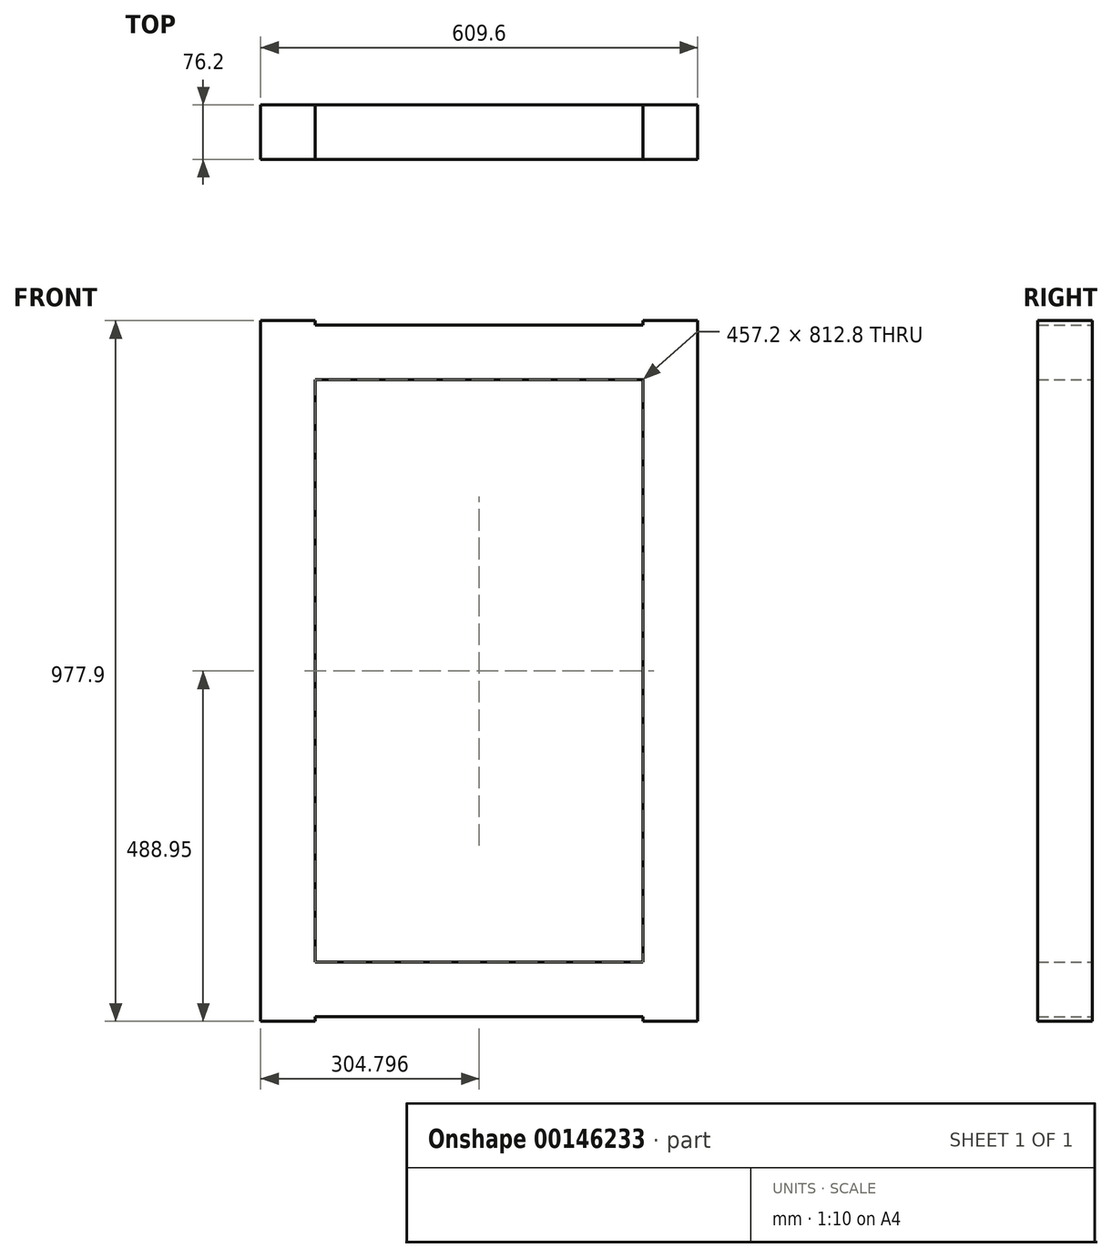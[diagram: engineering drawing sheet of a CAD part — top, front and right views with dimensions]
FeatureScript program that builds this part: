
annotation { "Feature Type Name" : "Feature", "Feature Type Description" : "" }
export const myFeature = defineFeature(function(context is Context, id is Id, definition is map)
    precondition{}
    {
        {
            var Q0;
            Q0=qCreatedBy(makeId("Top.planeOp"),FACE);
            var sketch = newSketch(context, id + "F0", { "sketchPlane" : qUnion([Q0])});
            skLineSegment(sketch, "E0.bottom", {"start": v(-224.13, 41.12) * mm, "end": v(233.07, 41.12) * mm});
            skLineSegment(sketch, "E0.top", {"start": v(-224.13, -35.08) * mm, "end": v(233.07, -35.08) * mm});
            skLineSegment(sketch, "E0.left", {"start": v(-224.13, 41.12) * mm, "end": v(-224.13, -35.08) * mm});
            skLineSegment(sketch, "E0.right", {"start": v(233.07, 41.12) * mm, "end": v(233.07, -35.08) * mm});
            skSolve(sketch);
        }
        {
            var Q0;
            Q0=makeQuery(id+"F0.imprint","IMPRINT",FACE,{"disambiguationData":[TD([[makeQuery(id+"F0.imprint","IMPRINT",EDGE,{"derivedFrom":sQuery(id+"F0.wireOp",EDGE,"E0.bottom")}),-1.0]])]});
            extrude(context, id + "F1", {"entities" : qUnion([Q0]), "depth" : 76.2 * mm});
        }
        {
            var Q0;
            Q0=makeQuery(id+"F1.opExtrude","SWEPT_FACE",FACE,{"disambiguationData":[OSD([sQuery(id+"F0.wireOp",EDGE,"E0.right")])]});
            extrude(context, id + "F2", {"entities" : qUnion([Q0]), "operationType" : NewBodyOperationType.ADD, "depth" : 152.4 * mm});
        }
        {
            var Q0;
            {var subQ0=sQuery(id+"F0.wireOp",EDGE,"E0.right");Q0=makeQuery(id+"F2.boolean.opBoolean","MERGE",FACE,{"derivedFrom":[makeQuery(id+"F1.opExtrude","CAP_FACE",FACE,{"disambiguationData":[OSD([sQuery(id+"F0.wireOp",EDGE,"E0.bottom"),sQuery(id+"F0.wireOp",EDGE,"E0.top"),sQuery(id+"F0.wireOp",EDGE,"E0.left"),subQ0])],"isStart":false}),makeQuery(id+"F2.opExtrude","SWEPT_FACE",FACE,{"disambiguationData":[OSD([subQ0]),TDD([makeQuery(id+"F1.opExtrude","CAP_EDGE",EDGE,{"disambiguationData":[OSD([subQ0])],"isStart":false})])]})]});}
            var sketch = newSketch(context, id + "F3", { "sketchPlane" : qUnion([Q0])});
            skLineSegment(sketch, "E1.bottom", {"start": v(385.47, -35.08) * mm, "end": v(309.27, -35.08) * mm});
            skLineSegment(sketch, "E1.top", {"start": v(385.47, 41.12) * mm, "end": v(309.27, 41.12) * mm});
            skLineSegment(sketch, "E1.left", {"start": v(385.47, -35.08) * mm, "end": v(385.47, 41.12) * mm});
            skLineSegment(sketch, "E1.right", {"start": v(309.27, -35.08) * mm, "end": v(309.27, 41.12) * mm});
            skSolve(sketch);
        }
        {
            var Q0;
            Q0=makeQuery(id+"F3.imprint","IMPRINT",FACE,{"disambiguationData":[TD([[makeQuery(id+"F3.imprint","IMPRINT",EDGE,{"derivedFrom":sQuery(id+"F3.wireOp",EDGE,"E1.bottom")}),1.0]])]});
            extrude(context, id + "F4", {"entities" : qUnion([Q0]), "operationType" : NewBodyOperationType.ADD, "depth" : 895.35 * mm});
        }
        {
            var Q0;
            {var subQ0=sQuery(id+"F0.wireOp",EDGE,"E0.right");Q0=makeQuery(id+"F2.boolean.opBoolean","MERGE",FACE,{"derivedFrom":[makeQuery(id+"F1.opExtrude","CAP_FACE",FACE,{"disambiguationData":[OSD([sQuery(id+"F0.wireOp",EDGE,"E0.bottom"),sQuery(id+"F0.wireOp",EDGE,"E0.top"),sQuery(id+"F0.wireOp",EDGE,"E0.left"),subQ0])],"isStart":true}),makeQuery(id+"F2.opExtrude","SWEPT_FACE",FACE,{"disambiguationData":[OSD([subQ0]),TDD([makeQuery(id+"F1.opExtrude","CAP_EDGE",EDGE,{"disambiguationData":[OSD([subQ0])],"isStart":true})])]})]});}
            var sketch = newSketch(context, id + "F5", { "sketchPlane" : qUnion([Q0])});
            skLineSegment(sketch, "E2.bottom", {"start": v(385.47, -41.12) * mm, "end": v(309.27, -41.12) * mm});
            skLineSegment(sketch, "E2.top", {"start": v(385.47, 35.08) * mm, "end": v(309.27, 35.08) * mm});
            skLineSegment(sketch, "E2.left", {"start": v(385.47, -41.12) * mm, "end": v(385.47, 35.08) * mm});
            skLineSegment(sketch, "E2.right", {"start": v(309.27, -41.12) * mm, "end": v(309.27, 35.08) * mm});
            skSolve(sketch);
        }
        {
            var Q0;
            Q0=makeQuery(id+"F5.imprint","IMPRINT",FACE,{"disambiguationData":[TD([[makeQuery(id+"F5.imprint","IMPRINT",EDGE,{"derivedFrom":sQuery(id+"F5.wireOp",EDGE,"E2.bottom")}),1.0]])]});
            extrude(context, id + "F11", {"entities" : qUnion([Q0]), "operationType" : NewBodyOperationType.ADD, "depth" : 6.35 * mm});
        }
        {
            var Q0;
            Q0=makeQuery(id+"F4.opExtrude","SWEPT_FACE",FACE,{"disambiguationData":[OSD([sQuery(id+"F3.wireOp",EDGE,"E1.right")])]});
            var sketch = newSketch(context, id + "F6", { "sketchPlane" : qUnion([Q0])});
            skLineSegment(sketch, "E3.bottom", {"start": v(35.08, 965.2) * mm, "end": v(-41.12, 965.2) * mm});
            skLineSegment(sketch, "E3.top", {"start": v(35.08, 889) * mm, "end": v(-41.12, 889) * mm});
            skLineSegment(sketch, "E3.left", {"start": v(35.08, 965.2) * mm, "end": v(35.08, 889) * mm});
            skLineSegment(sketch, "E3.right", {"start": v(-41.12, 965.2) * mm, "end": v(-41.12, 889) * mm});
            skSolve(sketch);
        }
        {
            var Q0;
            Q0=makeQuery(id+"F6.imprint","IMPRINT",FACE,{"disambiguationData":[TD([[makeQuery(id+"F6.imprint","IMPRINT",EDGE,{"derivedFrom":sQuery(id+"F6.wireOp",EDGE,"E3.bottom")}),1.0]])]});
            extrude(context, id + "F7", {"entities" : qUnion([Q0]), "operationType" : NewBodyOperationType.ADD, "depth" : 533.4 * mm});
        }
        {
            var Q0;
            Q0=makeQuery(id+"F7.opExtrude","SWEPT_FACE",FACE,{"disambiguationData":[OSD([sQuery(id+"F6.wireOp",EDGE,"E3.top")])]});
            var sketch = newSketch(context, id + "F8", { "sketchPlane" : qUnion([Q0])});
            skLineSegment(sketch, "E4.bottom", {"start": v(-224.13, 35.08) * mm, "end": v(-147.93, 35.08) * mm});
            skLineSegment(sketch, "E4.top", {"start": v(-224.13, -41.12) * mm, "end": v(-147.93, -41.12) * mm});
            skLineSegment(sketch, "E4.left", {"start": v(-224.13, 35.08) * mm, "end": v(-224.13, -41.12) * mm});
            skLineSegment(sketch, "E4.right", {"start": v(-147.93, 35.08) * mm, "end": v(-147.93, -41.12) * mm});
            skSolve(sketch);
        }
        {
            var Q0;
            Q0=makeQuery(id+"F8.imprint","IMPRINT",FACE,{"disambiguationData":[TD([[makeQuery(id+"F8.imprint","IMPRINT",EDGE,{"derivedFrom":sQuery(id+"F8.wireOp",EDGE,"E4.bottom")}),-1.0]])]});
            extrude(context, id + "F12", {"entities" : qUnion([Q0]), "operationType" : NewBodyOperationType.ADD, "depth" : 895.35 * mm});
        }
        {
            var Q0;
            Q0=makeQuery(id+"F7.opExtrude","SWEPT_FACE",FACE,{"disambiguationData":[OSD([sQuery(id+"F6.wireOp",EDGE,"E3.bottom")])]});
            var sketch = newSketch(context, id + "F9", { "sketchPlane" : qUnion([Q0])});
            skLineSegment(sketch, "E5.bottom", {"start": v(-224.13, 41.12) * mm, "end": v(-147.93, 41.12) * mm});
            skLineSegment(sketch, "E5.top", {"start": v(-224.13, -35.08) * mm, "end": v(-147.93, -35.08) * mm});
            skLineSegment(sketch, "E5.left", {"start": v(-224.13, 41.12) * mm, "end": v(-224.13, -35.08) * mm});
            skLineSegment(sketch, "E5.right", {"start": v(-147.93, 41.12) * mm, "end": v(-147.93, -35.08) * mm});
            skSolve(sketch);
        }
        {
            var Q0;
            Q0=makeQuery(id+"F9.imprint","IMPRINT",FACE,{"disambiguationData":[TD([[makeQuery(id+"F9.imprint","IMPRINT",EDGE,{"derivedFrom":sQuery(id+"F9.wireOp",EDGE,"E5.bottom")}),-1.0]])]});
            extrude(context, id + "F10", {"entities" : qUnion([Q0]), "operationType" : NewBodyOperationType.ADD, "depth" : 6.35 * mm});
        }
    });
